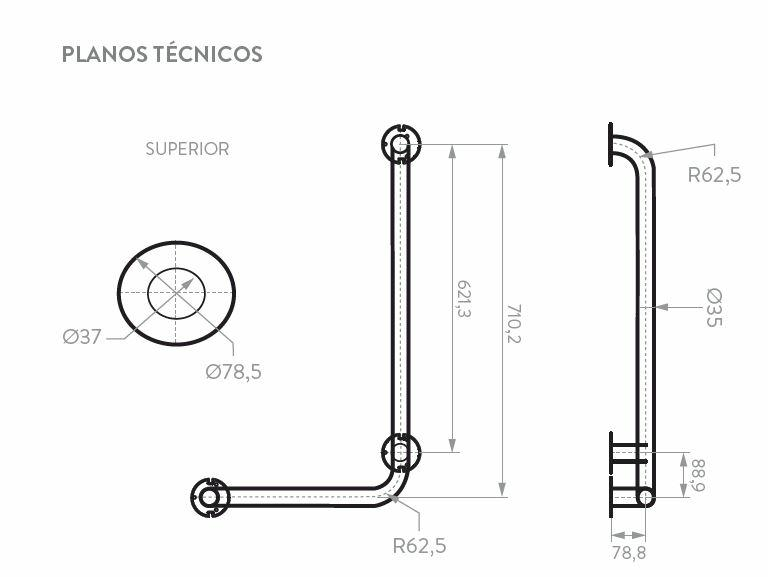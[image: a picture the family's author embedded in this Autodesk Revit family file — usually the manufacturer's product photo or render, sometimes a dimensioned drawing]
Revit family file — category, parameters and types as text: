
# Revit family: 706580001_Barra de Seguridad en L
name_source: partatom
category: Plumbing Fixtures
units: mm (PartAtom-declared; Revit-internal decimal feet)

## family parameters
Always vertical = Yes
Cut with Voids When Loaded = No
Host = Wall
OmniClass Number = 23.31.00.00
OmniClass Title = Plumbing Specific Products and Equipment
Part Type = Normal
Room Calculation Point = No
Round Connector Dimension = Use Diameter
Shared = No

## types (1)
- Type 1
    Alto = 710 mm
    Ancho = 461 mm  [stored 1.51247 ft]
    Capacidad de Funcionamiento = Soporta una carga hasta de 150 Kg.
    Creado por = BIMBAU
    Cuidado Y Limpieza = Para prolongar y preservar las cualidades del acero es vital que la limpieza profunda del producto se haga únicamente con agua y jabón suave y que en el secado y el brillo se utilice un paño de algodón limpio, dicha limpieza se recomienda 2 veces a la semana, y en zonas costeras a diario por la salinidad del ambiente. Por ningún motivo deben usarse elementos abrasivos, ácidos o disolventes para la limpieza del producto. (ácido muriático, ácido sulfúrico, yodo,
derivados del cloro, amoniaco, blanqueadores.) Los acabados pueden variar su comportamiento en zonas costeras y/o en ambientes corrosivos. En referencias satinadas limpie en el sentido del pulido del acero.
    Default Elevation = 0 mm  [stored 0 ft]
    Description = Elemento de mobiliario para el apoyo, seguridad y protección
de usuarios que acompaña la dirección de una circulación.
    Escudo Metálico = Material metálico, mayor durabilidad
y excelentes propiedades mecánicas.
    Fecha de creación = 8/04/2021
    Garantía = 1 Año
    Material = Corona_Acero inoxidable
    Profundidad = 79 mm
    Referencia = 706580001
    Resistencia = Corrosión, pelado y decoloración por agua.
    Sistema de Instalación = Fácil instalación por medio de chazos
y tornillos anclados a la pared que ofrecen gran seguridad.
    Tipo de instalación = Expuesto E.S.
    URL = https://corona.co
    Uso = Doméstico e institucional

note: [stored X ft] marks values corroborated as IEEE doubles in the binary element streams (Revit-internal decimal feet)

## geometry (parser evidence)
native form markers: Sweep x3
no freeform markers — native parametric forms only
